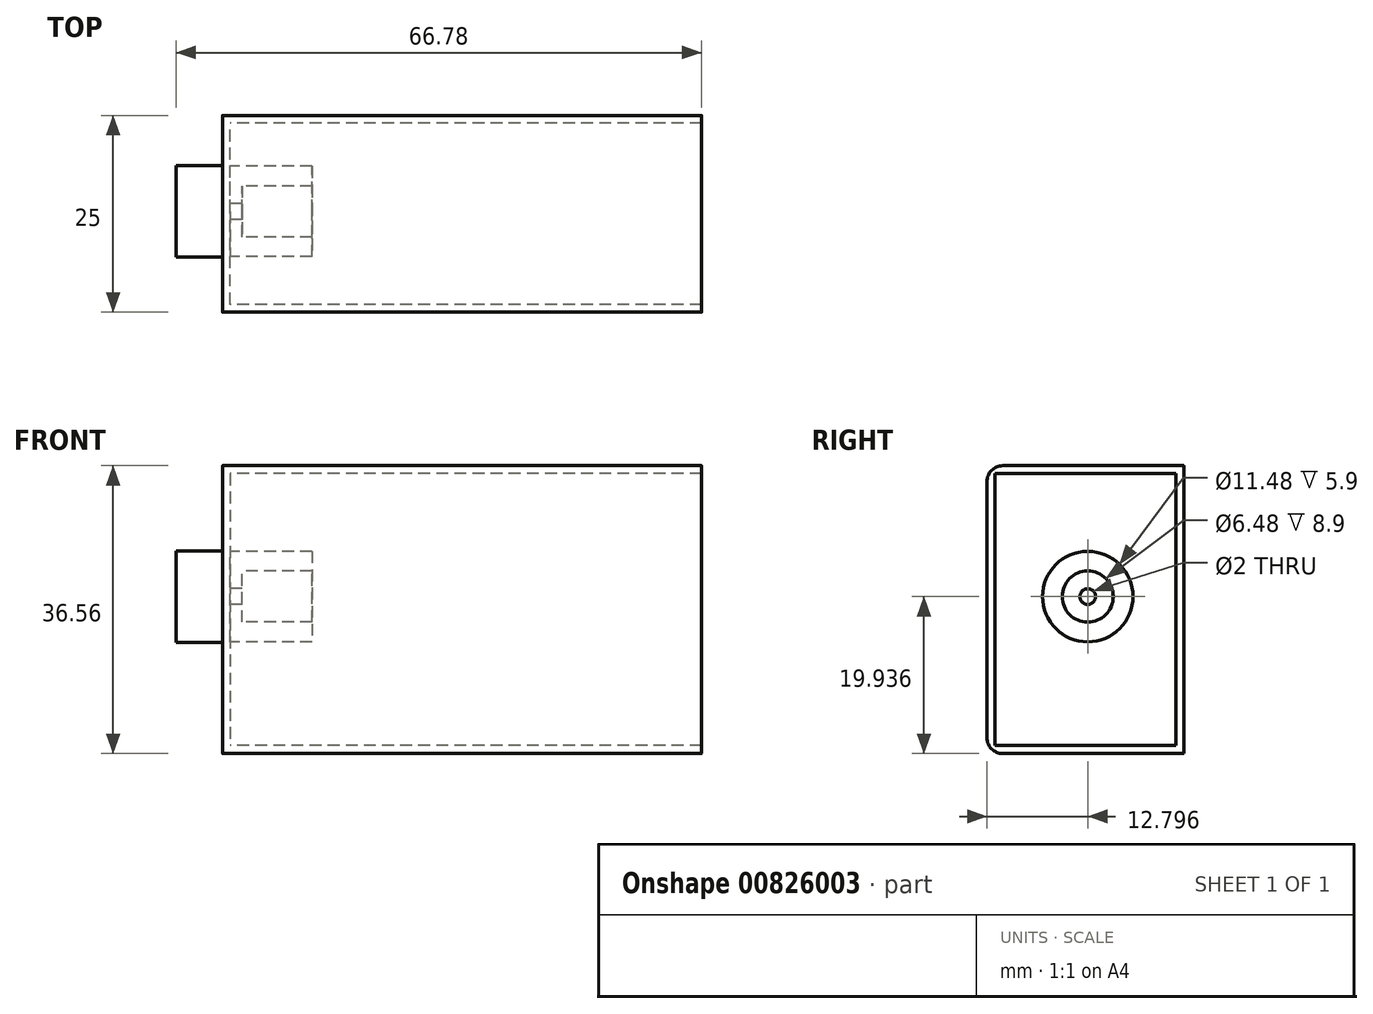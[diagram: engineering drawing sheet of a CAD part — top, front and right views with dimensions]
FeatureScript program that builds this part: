
annotation { "Feature Type Name" : "Feature", "Feature Type Description" : "" }
export const myFeature = defineFeature(function(context is Context, id is Id, definition is map)
    precondition{}
    {
        {
            var Q0;
            Q0=qCreatedBy(makeId("Front.planeOp"),FACE);
            var sketch = newSketch(context, id + "F0", { "sketchPlane" : qUnion([Q0])});
            skLineSegment(sketch, "E0.bottom", {"start": v(0, 0) * mm, "end": v(-60.88, 0) * mm});
            skLineSegment(sketch, "E0.top", {"start": v(0, -36.56) * mm, "end": v(-60.88, -36.56) * mm});
            skLineSegment(sketch, "E0.left", {"start": v(0, 0) * mm, "end": v(0, -36.56) * mm});
            skLineSegment(sketch, "E0.right", {"start": v(-60.88, 0) * mm, "end": v(-60.88, -36.56) * mm});
            skSolve(sketch);
        }
        {
            var Q0;
            Q0=makeQuery(id+"F0.imprint","IMPRINT",FACE,{"disambiguationData":[TD([[makeQuery(id+"F0.imprint","IMPRINT",EDGE,{"derivedFrom":sQuery(id+"F0.wireOp",EDGE,"E0.bottom")}),1.0]])]});
            extrude(context, id + "F1", {"entities" : qUnion([Q0]), "depth" : 25 * mm, "offsetDistance" : 25 * mm});
        }
        {
            var Q0;
            Q0=makeQuery(id+"F1.opExtrude","SWEPT_FACE",FACE,{"disambiguationData":[OSD([sQuery(id+"F0.wireOp",EDGE,"E0.left")])]});
            shell(context, id + "F2", {"entities" : qUnion([Q0]), "thickness" : 1 * mm});
        }
        {
            var Q0;
            Q0=makeQuery(id+"F1.opExtrude","SWEPT_FACE",FACE,{"disambiguationData":[OSD([sQuery(id+"F0.wireOp",EDGE,"E0.right")])]});
            var sketch = newSketch(context, id + "F3", { "sketchPlane" : qUnion([Q0])});
            skCircle(sketch, "E1", {"center": v(12.2, -16.62) * mm, "radius": 5.8 * mm});
            skCircle(sketch, "E2", {"center": v(12.2, -16.62) * mm, "radius": 5.74 * mm});
            skSolve(sketch);
        }
        {
            var Q0;
            Q0 = qSketchRegion(id + "F3", true);
            extrude(context, id + "F4", {"entities" : qUnion([Q0]), "operationType" : NewBodyOperationType.ADD, "depth" : 5.9 * mm, "offsetDistance" : 25 * mm});
        }
        {
            var Q0;
            Q0=makeQuery(id+"F4.boolean.opBoolean","SPLIT",FACE,{"disambiguationData":[TD([makeQuery(id+"F4.opExtrude","SWEPT_FACE",FACE,{"disambiguationData":[OSD([sQuery(id+"F3.wireOp",EDGE,"E2")])]})])],"derivedFrom":makeQuery(id+"F1.opExtrude","SWEPT_FACE",FACE,{"disambiguationData":[OSD([sQuery(id+"F0.wireOp",EDGE,"E0.right")])]})});
            extrude(context, id + "F5", {"entities" : qUnion([Q0]), "operationType" : NewBodyOperationType.ADD, "oppositeDirection" : true, "depth" : 11.4 * mm, "offsetDistance" : 25 * mm});
        }
        {
            var Q0;
            Q0=makeQuery(id+"F5.opExtrude","CAP_FACE",FACE,{"disambiguationData":[OSD([sQuery(id+"F0.wireOp",EDGE,"E0.right")])],"isStart":false});
            shell(context, id + "F6", {"entities" : qUnion([Q0]), "thickness" : 2.5 * mm});
        }
        {
            var Q0;
            Q0=makeQuery(id+"F6.opShell","OFFSET_FACE",FACE,{"disambiguationData":[OSD([sQuery(id+"F0.wireOp",EDGE,"E0.right")])]});
            shell(context, id + "F7", {"entities" : qUnion([Q0]), "thickness" : 2.5 * mm});
        }
        {
            var Q0;
            Q0=makeQuery(id+"F4.boolean.opBoolean","SPLIT",FACE,{"disambiguationData":[TD([makeQuery(id+"F4.opExtrude","SWEPT_FACE",FACE,{"disambiguationData":[OSD([sQuery(id+"F3.wireOp",EDGE,"E2")])]})])],"derivedFrom":makeQuery(id+"F1.opExtrude","SWEPT_FACE",FACE,{"disambiguationData":[OSD([sQuery(id+"F0.wireOp",EDGE,"E0.right")])]})});
            var sketch = newSketch(context, id + "F8", { "sketchPlane" : qUnion([Q0])});
            skCircle(sketch, "E3", {"center": v(12.2, -16.62) * mm, "radius": 4.47 * mm});
            skSolve(sketch);
        }
        {
            var Q0;
            Q0=sQuery(id+"F8.wireOp",VERTEX,"E3.center");
            var Q1;
            Q1=makeQuery(id+"F1.opExtrude","SWEPT_BODY",BODY,{"disambiguationData":[OSD([sQuery(id+"F0.wireOp",EDGE,"E0.bottom"),sQuery(id+"F0.wireOp",EDGE,"E0.top"),sQuery(id+"F0.wireOp",EDGE,"E0.left"),sQuery(id+"F0.wireOp",EDGE,"E0.right")])]});
            hole(context, id + "F9", {"style" : HoleStyle.SIMPLE, "endStyle" : HoleEndStyle.THROUGH, "holeDiameter" : 2 * mm, "majorDiameter" : 5 * mm, "isTappedThrough" : true, "tappedDepth" : 12 * mm, "tapClearance" : 3, "locations" : qUnion([Q0]), "scope" : qUnion([Q1])});
        }
        {
            var Q0;
            Q0=makeQuery(id+"F1.opExtrude","CAP_EDGE",EDGE,{"disambiguationData":[OSD([sQuery(id+"F0.wireOp",EDGE,"E0.top")])],"isStart":false});
            var Q1;
            Q1=makeQuery(id+"F1.opExtrude","CAP_EDGE",EDGE,{"disambiguationData":[OSD([sQuery(id+"F0.wireOp",EDGE,"E0.bottom")])],"isStart":false});
            fillet(context, id + "F10", {"entities" : qUnion([Q0, Q1]), "radius" : 2 * mm, "tangentPropagation" : true, "allowEdgeOverflow" : false});
        }
        {
            var Q0;
            Q0=makeQuery(id+"F1.opExtrude","CAP_EDGE",EDGE,{"disambiguationData":[OSD([sQuery(id+"F0.wireOp",EDGE,"E0.top")])],"isStart":true});
            var Q1;
            Q1=makeQuery(id+"F1.opExtrude","CAP_EDGE",EDGE,{"disambiguationData":[OSD([sQuery(id+"F0.wireOp",EDGE,"E0.bottom")])],"isStart":true});
            fillet(context, id + "F11", {"entities" : qUnion([Q0, Q1]), "radius" : 0.02 * mm, "tangentPropagation" : true, "allowEdgeOverflow" : false});
        }
        {
            var Q0;
            {var subQ0=sQuery(id+"F0.wireOp",EDGE,"E0.top");Q0=makeQuery(id+"F11.opFillet","BLEND_EDGE",EDGE,{"blendedFrom":[makeQuery(id+"F1.opExtrude","CAP_EDGE",EDGE,{"disambiguationData":[OSD([subQ0])],"isStart":true}),makeQuery(id+"F1.opExtrude","SWEPT_FACE",FACE,{"disambiguationData":[OSD([subQ0])]})],"blendedInto":[makeQuery(id+"F1.opExtrude","SWEPT_FACE",FACE,{"disambiguationData":[OSD([subQ0])]})]});}
            var Q1;
            {var subQ0=sQuery(id+"F0.wireOp",EDGE,"E0.bottom");Q1=makeQuery(id+"F11.opFillet","BLEND_EDGE",EDGE,{"blendedFrom":[makeQuery(id+"F1.opExtrude","CAP_EDGE",EDGE,{"disambiguationData":[OSD([subQ0])],"isStart":true}),makeQuery(id+"F1.opExtrude","CAP_FACE",FACE,{"disambiguationData":[OSD([subQ0,sQuery(id+"F0.wireOp",EDGE,"E0.top"),sQuery(id+"F0.wireOp",EDGE,"E0.left"),sQuery(id+"F0.wireOp",EDGE,"E0.right")])],"isStart":true})],"blendedInto":[makeQuery(id+"F1.opExtrude","CAP_FACE",FACE,{"disambiguationData":[OSD([subQ0,sQuery(id+"F0.wireOp",EDGE,"E0.top"),sQuery(id+"F0.wireOp",EDGE,"E0.left"),sQuery(id+"F0.wireOp",EDGE,"E0.right")])],"isStart":true})]});}
            var Q2;
            Q2=makeQuery(id+"F1.opExtrude","CAP_EDGE",EDGE,{"disambiguationData":[OSD([sQuery(id+"F0.wireOp",EDGE,"E0.left")])],"isStart":true});
            var Q3;
            Q3=makeQuery(id+"F1.opExtrude","CAP_EDGE",EDGE,{"disambiguationData":[OSD([sQuery(id+"F0.wireOp",EDGE,"E0.right")])],"isStart":true});
            fillet(context, id + "F12", {"entities" : qUnion([Q0, Q1, Q2, Q3]), "radius" : 0.02 * mm, "tangentPropagation" : true, "allowEdgeOverflow" : false});
        }
    });
